# Revit family: Lavatory-Grohe-Darin-28951000
name_source: partatom
category: Plumbing Fixtures
revit_build: Autodesk Revit 2014 (Build: 20130308_1515(x64)
units: mm (PartAtom-declared; Revit-internal decimal feet)

## types (1)
- 28951000
    Assembly Code = D2030
    CW Connection = No
    CWFU = 0
    Default Elevation = 0"
    Description = Lavatory Grid Waste
    Finish = Metal-Grohe-000-StarLight Chrome
    HW Connection = No
    HWFU = 0
    Height = 6 1/2"
    Manufacturer = GROHE
    Material = Metal-Grohe-000-StarLight Chrome
    Model = 28951000
    Price = Prices may vary. Please consult Manufacturer Representative for most up-to-date price list.
    Product Page URL = https://www.grohe.ca
    URL = https://www.grohe.ca
    Vent Connection = No
    WFU = 2
    Waste Connection = Yes
    Waste Connection Diameter = 1 1/4"
    Waste Connection Radius = 5/8"
    Width = 2 3/16"

## geometry (parser evidence)
native form markers: Sweep x2
no freeform markers — native parametric forms only
